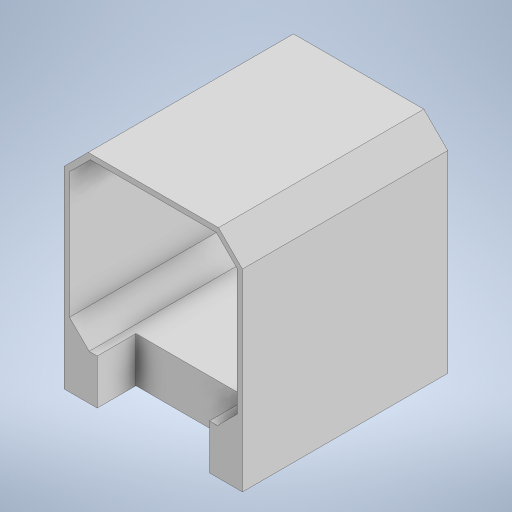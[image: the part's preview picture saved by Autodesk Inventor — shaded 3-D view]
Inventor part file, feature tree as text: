
AUTODESK INVENTOR PART (.ipt)
format: ipt  version: 2024.2 (Build 282272000, 272)  size: 620,544 bytes
history: native  units: mm
features: reference x37, extrude x4, sketch x4, other x3, projected_geometry x2
ambient origin geometry x8: Origin, YZ Plane, XZ Plane, XY Plane, X Axis, Y Axis, Z Axis, Center Point
bodies: Solid1 (feature_tree)
feature tree (50):
  extrude  "Extrusion1"  Depth=43.0mm TaperAngle=0.0deg
  extrude  "Extrusion2"  Depth=9.0mm TaperAngle=0.0deg
  extrude  "Extrusion3"  [1 undecoded]
  extrude  "Extrusion5"  [1 undecoded]
  sketch  "Sketch1"  dims[d0=5.0mm d1=0.0mm d2=43.0mm d3=0.0mm]
  reference  "Reference1"
  reference  "Reference2"
  reference  "Reference3"
  reference  "Reference4"
  reference  "Reference5"
  reference  "Reference6"
  reference  "Reference7"
  reference  "Reference8"
  reference  "Reference9"
  reference  "Reference10"
  reference  "Reference11"
  reference  "Reference12"
  reference  "Reference13"
  reference  "Reference14"
  reference  "Reference15"
  reference  "Reference16"
  reference  "Reference17"
  reference  "Reference18"
  reference  "Reference19"
  reference  "Reference20"
  reference  "Reference21"
  sketch  "Sketch2"  dims[d4=10.0mm d5=0.0mm d10=9.0mm d11=0.0mm]
  reference  "Reference22"
  reference  "Reference23"
  reference  "Reference24"
  reference  "Reference25"
  reference  "Reference26"
  projected_geometry  "Projected Loop1"
  reference  "Reference27"
  reference  "Reference28"
  reference  "Reference29"
  reference  "Reference30"
  reference  "Reference31"
  reference  "Reference32"
  sketch  "Sketch3"
  reference  "Reference33"
  reference  "Reference34"
  reference  "Reference35"
  reference  "Reference36"
  projected_geometry  "Projected Loop2"
  reference  "Reference37"
  sketch  "Sketch4"
  other  "<userpath>\Desktop\meca_robotbebou\embasev2\embasev2.iam"
  other  "embasev2.iam"
  other  "support_moteurv3:1"
note: 2 required parameter values undecoded (feature->parameter linkage not recoverable at this tier; creation-order binding heuristic only, values carry confidence <= 0.55)
